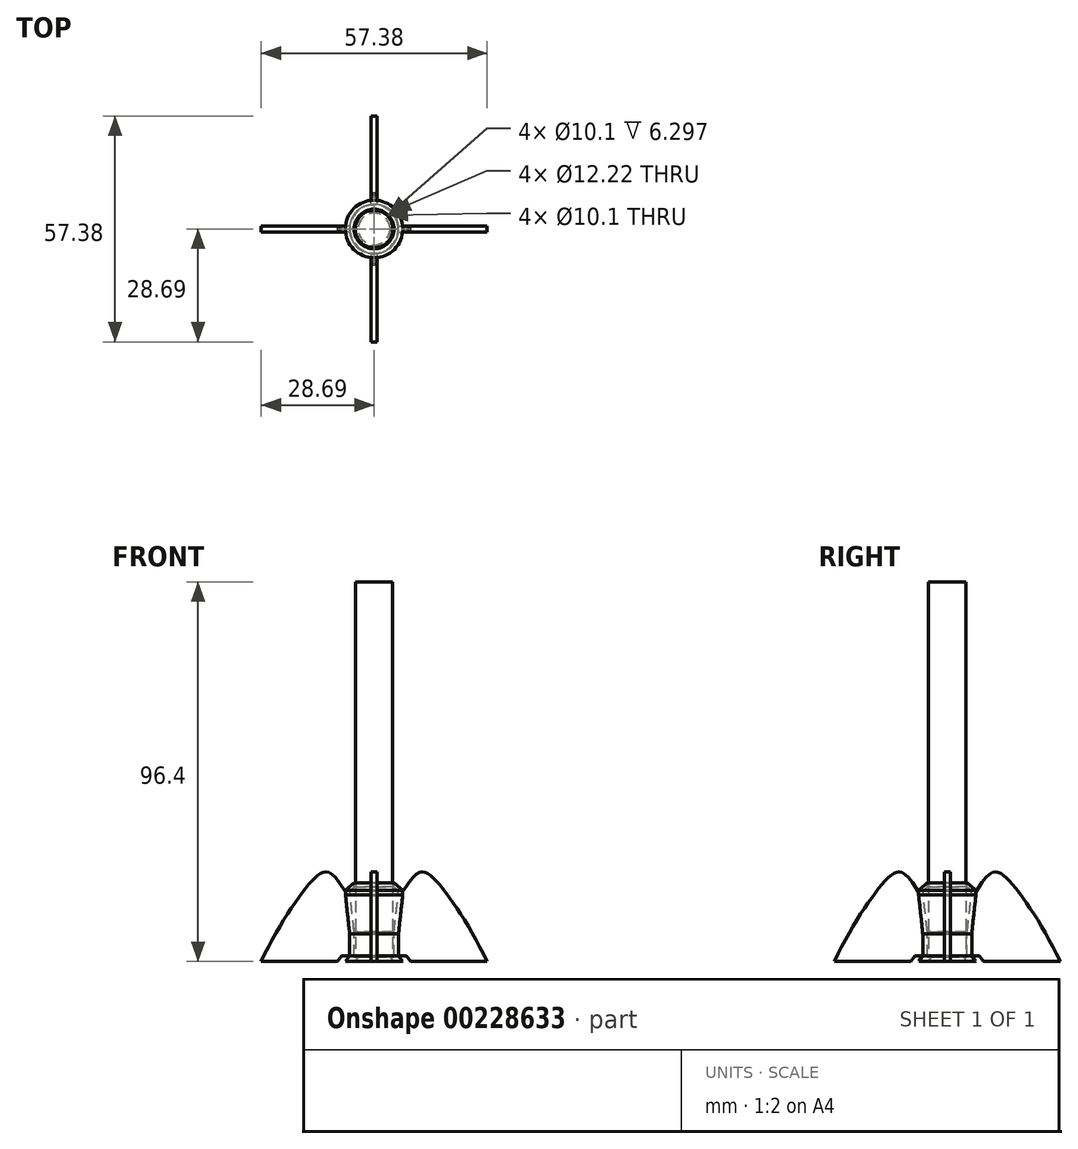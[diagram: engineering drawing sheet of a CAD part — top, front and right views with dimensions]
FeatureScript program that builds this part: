
annotation { "Feature Type Name" : "Feature", "Feature Type Description" : "" }
export const myFeature = defineFeature(function(context is Context, id is Id, definition is map)
    precondition{}
    {
        {
            var Q0;
            Q0=qCreatedBy(makeId("Top.planeOp"),FACE);
            var sketch = newSketch(context, id + "F0", { "sketchPlane" : qUnion([Q0])});
            skCircle(sketch, "E0", {"center": v(0, 0) * mm, "radius": 4.75 * mm});
            skSolve(sketch);
        }
        {
            var Q0;
            Q0=qCreatedBy(makeId("Front.planeOp"),FACE);
            var sketch = newSketch(context, id + "F1", { "sketchPlane" : qUnion([Q0])});
            skLineSegment(sketch, "E1", {"start": v(-4.75, 31.9) * mm, "end": v(-4.75, 0) * mm, "construction": true});
            skLineSegment(sketch, "E2", {"start": v(-4.75, 0) * mm, "end": v(0, 0) * mm});
            skLineSegment(sketch, "E3", {"start": v(-5.05, 18.6) * mm, "end": v(-5.05, 17.49) * mm});
            skLineSegment(sketch, "E4", {"start": v(-5.05, -0.2) * mm, "end": v(-4.05, -0.2) * mm});
            skLineSegment(sketch, "E5", {"start": v(0, -0.2) * mm, "end": v(0, -1.4) * mm});
            skLineSegment(sketch, "E6", {"start": v(-4.87, -1.4) * mm, "end": v(-6.25, -1.4) * mm});
            skLineSegment(sketch, "E7", {"start": v(-6.25, 0) * mm, "end": v(-6.25, 5.55) * mm});
            skLineSegment(sketch, "E8", {"start": v(-7.31, 15.52) * mm, "end": v(-7.31, 16.66) * mm});
            skLineSegment(sketch, "E9", {"start": v(-7.31, 16.66) * mm, "end": v(-5.05, 18.6) * mm});
            skLineSegment(sketch, "E10", {"start": v(-4.87, -1.4) * mm, "end": v(-45.41, -1.4) * mm, "construction": true});
            skLineSegment(sketch, "E11", {"start": v(-5.05, 6.1) * mm, "end": v(-6.11, 15.43) * mm});
            skLineSegment(sketch, "E12", {"start": v(-6.11, 15.43) * mm, "end": v(-6.11, 16.58) * mm});
            skLineSegment(sketch, "E13", {"start": v(-6.11, 16.58) * mm, "end": v(-5.05, 17.49) * mm});
            skLineSegment(sketch, "E14", {"start": v(-7.31, 15.52) * mm, "end": v(-6.25, 5.55) * mm});
            skLineSegment(sketch, "E15.trimOffspring", {"start": v(-5.05, 6.1) * mm, "end": v(-5.05, -0.2) * mm});
            skLineSegment(sketch, "E16", {"start": v(-6.25, -1.4) * mm, "end": v(-7.2, -1.4) * mm});
            skLineSegment(sketch, "E17", {"start": v(-7.2, -1.4) * mm, "end": v(-6.25, 0) * mm});
            skLineSegment(sketch, "E18", {"start": v(-4.87, -1.4) * mm, "end": v(-4.05, -0.2) * mm});
            skSolve(sketch);
        }
        {
            var Q0;
            Q0=makeQuery(id+"F0.imprint","IMPRINT",FACE,{"disambiguationData":[TD([[makeQuery(id+"F0.imprint","IMPRINT",EDGE,{"derivedFrom":sQuery(id+"F0.wireOp",EDGE,"E0")}),1.0]])]});
            extrude(context, id + "F2", {"entities" : qUnion([Q0]), "depth" : 95 * mm});
        }
        {
            var Q0;
            Q0=qCreatedBy(makeId("Front.planeOp"),FACE);
            var sketch = newSketch(context, id + "F3", { "sketchPlane" : qUnion([Q0])});
            skLineSegment(sketch, "E19", {"start": v(-5.57, 0) * mm, "end": v(-8.2, 0) * mm});
            skLineSegment(sketch, "E20", {"start": v(-8.2, 0) * mm, "end": v(-9.21, -1.4) * mm});
            skLineSegment(sketch, "E21", {"start": v(-8.85, 18.68) * mm, "end": v(-6.72, 15.48) * mm});
            skLineSegment(sketch, "E22", {"start": v(-9.21, -1.4) * mm, "end": v(-28.69, -1.4) * mm});
            skLineSegment(sketch, "E23", {"start": v(-5.57, 0) * mm, "end": v(-4.92, 0) * mm});
            skLineSegment(sketch, "E24", {"start": v(-5.55, 5.92) * mm, "end": v(-5.57, 0) * mm});
            skFitSpline(sketch, "E25", {"points": [v(-8.85, 18.68) * mm, v(-14.63, 20.13) * mm, v(-28.69, -1.4) * mm], "startDerivative": vector(-24.13, 32.55) * mm, "endDerivative": vector(-21.11, -43.49) * mm});
            skFitSpline(sketch, "E26.4", {"points": [v(-10.5, 17.62) * mm, v(-10.52, 17.6) * mm, v(-10.54, 17.59) * mm, v(-10.58, 17.57) * mm, v(-10.6, 17.56) * mm, v(-10.62, 17.55) * mm, v(-10.62, 17.54) * mm, v(-10.63, 17.53) * mm, v(-10.63, 17.54) * mm, v(-10.63, 17.53) * mm, v(-10.63, 17.53) * mm, v(-10.64, 17.53) * mm, v(-10.64, 17.53) * mm, v(-10.65, 17.53) * mm, v(-10.66, 17.51) * mm, v(-10.7, 17.5) * mm, v(-10.74, 17.46) * mm, v(-10.84, 17.38) * mm, v(-11.04, 17.2) * mm, v(-11.3, 16.95) * mm, v(-11.55, 16.71) * mm, v(-11.8, 16.47) * mm, v(-12.24, 16) * mm, v(-12.91, 15.25) * mm, v(-13.77, 14.23) * mm, v(-14.67, 13.09) * mm, v(-15.6, 11.84) * mm, v(-16.57, 10.48) * mm, v(-17.55, 9.03) * mm, v(-18.88, 6.97) * mm, v(-20.56, 4.18) * mm, v(-22.58, 0.53) * mm, v(-23.9, -2.07) * mm, v(-24.55, -3.4) * mm]});
            skLineSegment(sketch, "E26.5", {"start": v(-9.24, 3.2) * mm, "end": v(-21.09, 3.2) * mm});
            skLineSegment(sketch, "E27", {"start": v(-9.24, 3.2) * mm, "end": v(-7.12, 5.32) * mm});
            skLineSegment(sketch, "E28", {"start": v(-7.12, 5.32) * mm, "end": v(-7.76, 11.35) * mm});
            skLineSegment(sketch, "E29", {"start": v(-7.76, 11.35) * mm, "end": v(-11.77, 16.5) * mm});
            skLineSegment(sketch, "E30", {"start": v(-5.55, 5.92) * mm, "end": v(-6.72, 15.48) * mm});
            skSolve(sketch);
        }
        {
            var Q0;
            Q0 = qSketchRegion(id + "F1", true);
            var Q1;
            Q1=sQuery(id+"F1.wireOp",EDGE,"E5");
            revolve(context, id + "F4", {"entities" : qUnion([Q0]), "axis" : qUnion([Q1]), "revolveType" : RevolveType.FULL});
        }
        {
            var Q0;
            Q0=makeQuery(id+"F3.imprint","IMPRINT",FACE,{"disambiguationData":[TD([[makeQuery(id+"F3.imprint","IMPRINT",EDGE,{"derivedFrom":sQuery(id+"F3.wireOp",EDGE,"E19")}),-1.0]])]});
            extrude(context, id + "F5", {"entities" : qUnion([Q0]), "operationType" : NewBodyOperationType.ADD, "endBound" : BoundingType.SYMMETRIC, "depth" : 1.5 * mm});
        }
        {
            var Q0;
            Q0=makeQuery(id+"F4.opRevolve","SWEPT_BODY",BODY,{"disambiguationData":[OSD([sQuery(id+"F1.wireOp",EDGE,"E3"),sQuery(id+"F1.wireOp",EDGE,"E4"),sQuery(id+"F1.wireOp",EDGE,"E5"),sQuery(id+"F1.wireOp",EDGE,"E6"),sQuery(id+"F1.wireOp",EDGE,"E7"),sQuery(id+"F1.wireOp",EDGE,"E8"),sQuery(id+"F1.wireOp",EDGE,"E9"),sQuery(id+"F1.wireOp",EDGE,"E11"),sQuery(id+"F1.wireOp",EDGE,"E12"),sQuery(id+"F1.wireOp",EDGE,"E13"),sQuery(id+"F1.wireOp",EDGE,"E14"),sQuery(id+"F1.wireOp",EDGE,"E15.trimOffspring")])]});
            var Q1;
            Q1=makeQuery(id+"F4.opRevolve","SWEPT_FACE",FACE,{"disambiguationData":[OSD([sQuery(id+"F1.wireOp",EDGE,"E14")])]});
            circularPattern(context, id + "F6", {"entities" : qUnion([Q0]), "axis" : qUnion([Q1]), "angle" : 360 * degree, "instanceCount" : 4, "equalSpace" : true});
        }
        {
            var Q0;
            Q0=makeQuery(id+"F2.opExtrude","SWEPT_BODY",BODY,{"disambiguationData":[OSD([sQuery(id+"F0.wireOp",EDGE,"E0")])]});
            var Q1;
            Q1=makeQuery(id+"F4.opRevolve","SWEPT_BODY",BODY,{"disambiguationData":[OSD([sQuery(id+"F1.wireOp",EDGE,"E3"),sQuery(id+"F1.wireOp",EDGE,"E4"),sQuery(id+"F1.wireOp",EDGE,"E6"),sQuery(id+"F1.wireOp",EDGE,"E7"),sQuery(id+"F1.wireOp",EDGE,"E8"),sQuery(id+"F1.wireOp",EDGE,"E9"),sQuery(id+"F1.wireOp",EDGE,"E11"),sQuery(id+"F1.wireOp",EDGE,"E12"),sQuery(id+"F1.wireOp",EDGE,"E13"),sQuery(id+"F1.wireOp",EDGE,"E14"),sQuery(id+"F1.wireOp",EDGE,"E15.trimOffspring"),sQuery(id+"F1.wireOp",EDGE,"E16"),sQuery(id+"F1.wireOp",EDGE,"E17"),sQuery(id+"F1.wireOp",EDGE,"E18")])]});
            var Q2;
            Q2=makeQuery(id+"F6.opPattern","COPY",BODY,{"derivedFrom":makeQuery(id+"F4.opRevolve","SWEPT_BODY",BODY,{"disambiguationData":[OSD([sQuery(id+"F1.wireOp",EDGE,"E3"),sQuery(id+"F1.wireOp",EDGE,"E4"),sQuery(id+"F1.wireOp",EDGE,"E6"),sQuery(id+"F1.wireOp",EDGE,"E7"),sQuery(id+"F1.wireOp",EDGE,"E8"),sQuery(id+"F1.wireOp",EDGE,"E9"),sQuery(id+"F1.wireOp",EDGE,"E11"),sQuery(id+"F1.wireOp",EDGE,"E12"),sQuery(id+"F1.wireOp",EDGE,"E13"),sQuery(id+"F1.wireOp",EDGE,"E14"),sQuery(id+"F1.wireOp",EDGE,"E15.trimOffspring"),sQuery(id+"F1.wireOp",EDGE,"E16"),sQuery(id+"F1.wireOp",EDGE,"E17"),sQuery(id+"F1.wireOp",EDGE,"E18")])]}),"instanceName":"1"});
            var Q3;
            Q3=makeQuery(id+"F6.opPattern","COPY",BODY,{"derivedFrom":makeQuery(id+"F4.opRevolve","SWEPT_BODY",BODY,{"disambiguationData":[OSD([sQuery(id+"F1.wireOp",EDGE,"E3"),sQuery(id+"F1.wireOp",EDGE,"E4"),sQuery(id+"F1.wireOp",EDGE,"E6"),sQuery(id+"F1.wireOp",EDGE,"E7"),sQuery(id+"F1.wireOp",EDGE,"E8"),sQuery(id+"F1.wireOp",EDGE,"E9"),sQuery(id+"F1.wireOp",EDGE,"E11"),sQuery(id+"F1.wireOp",EDGE,"E12"),sQuery(id+"F1.wireOp",EDGE,"E13"),sQuery(id+"F1.wireOp",EDGE,"E14"),sQuery(id+"F1.wireOp",EDGE,"E15.trimOffspring"),sQuery(id+"F1.wireOp",EDGE,"E16"),sQuery(id+"F1.wireOp",EDGE,"E17"),sQuery(id+"F1.wireOp",EDGE,"E18")])]}),"instanceName":"2"});
            var Q4;
            Q4=makeQuery(id+"F6.opPattern","COPY",BODY,{"derivedFrom":makeQuery(id+"F4.opRevolve","SWEPT_BODY",BODY,{"disambiguationData":[OSD([sQuery(id+"F1.wireOp",EDGE,"E3"),sQuery(id+"F1.wireOp",EDGE,"E4"),sQuery(id+"F1.wireOp",EDGE,"E6"),sQuery(id+"F1.wireOp",EDGE,"E7"),sQuery(id+"F1.wireOp",EDGE,"E8"),sQuery(id+"F1.wireOp",EDGE,"E9"),sQuery(id+"F1.wireOp",EDGE,"E11"),sQuery(id+"F1.wireOp",EDGE,"E12"),sQuery(id+"F1.wireOp",EDGE,"E13"),sQuery(id+"F1.wireOp",EDGE,"E14"),sQuery(id+"F1.wireOp",EDGE,"E15.trimOffspring"),sQuery(id+"F1.wireOp",EDGE,"E16"),sQuery(id+"F1.wireOp",EDGE,"E17"),sQuery(id+"F1.wireOp",EDGE,"E18")])]}),"instanceName":"3"});
            booleanBodies(context, id + "F7", {"operationType" : BooleanOperationType.SUBTRACTION, "tools" : qUnion([Q0]), "targets" : qUnion([Q1, Q2, Q3, Q4]), "keepTools" : true});
        }
    });
